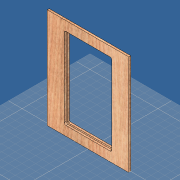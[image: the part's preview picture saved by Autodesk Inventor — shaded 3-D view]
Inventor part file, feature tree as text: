
AUTODESK INVENTOR PART (.ipt)
format: ipt  version: 2019 (Build 230136000, 136)  size: 151,552 bytes
history: native  units: mm
features: extrude x2, other x1, sketch x1
ambient origin geometry x8: Origin, YZ Plane, XZ Plane, XY Plane, X Axis, Y Axis, Z Axis, Center Point
bodies: Volumenkörper1 (feature_tree)
feature tree (4):
  other  "<userpath>\OneDrive\Dokumente\Inventor\Absauganlage\Absauganlage_Params.xlsx"
  sketch  "Skizze1"  dims[d0=140.0mm d1=240.0mm d2=5.0mm d3=232.0mm d4=132.0mm d5=2.0mm d6=128.0mm d7=228.0mm d8=2.0mm d11=240.0mm d12=295.0mm d13=210.0mm d14=265.0mm d15=6.0mm d16=0.0mm d17=6.0mm d18=0.0mm]
  extrude  "Extrusion1"  Depth=240.0mm
  extrude  "Extrusion2"  Depth=295.0mm
